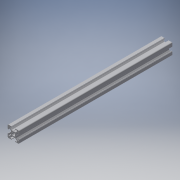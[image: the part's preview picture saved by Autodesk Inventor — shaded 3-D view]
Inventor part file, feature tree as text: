
AUTODESK INVENTOR PART (.ipt)
format: ipt  version: 2017 (Build 210142000, 142)  size: 308,736 bytes
history: native  units: in
note: dims shown in document units (in); Inventor stores cm internally (conversion verified against a paired STEP export)
features: other x3, extrude x1, sketch x1
ambient origin geometry x8: Origin, YZ Plane, XZ Plane, XY Plane, X Axis, Y Axis, Z Axis, Center Point
bodies: Solid1 (feature_tree)
feature tree (5):
  other  "Blocks"
  extrude  "Extrusion1"  Depth=1.0in
  sketch  "Sketch1"  dims[d1=0.0in d13=1.0in d14=1.0in]
  other  "20x20"
  other  "20x20:1"
